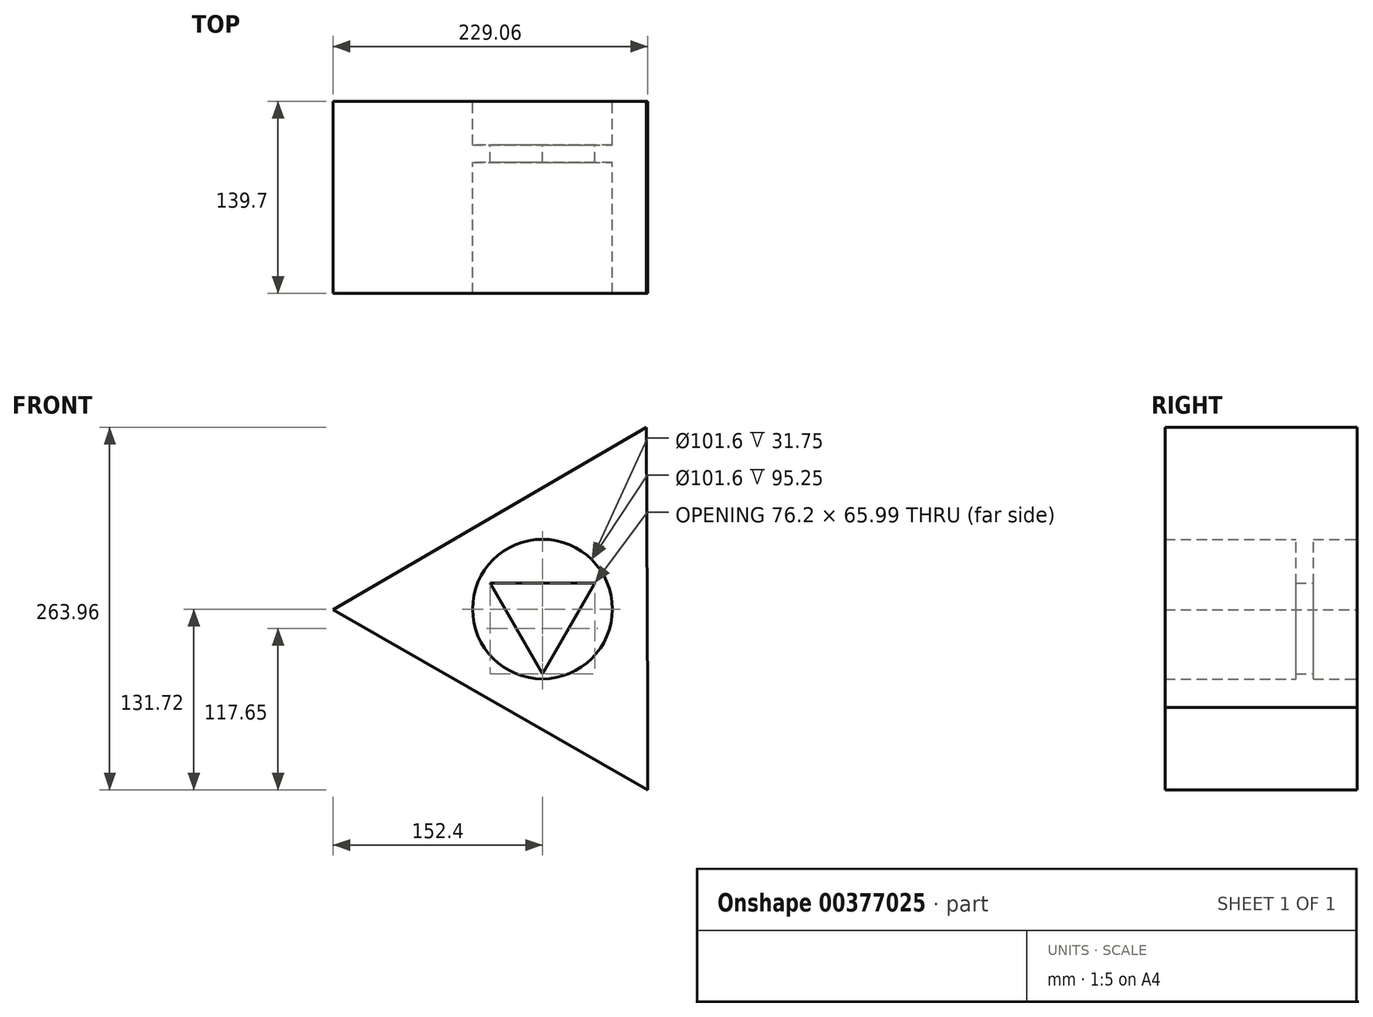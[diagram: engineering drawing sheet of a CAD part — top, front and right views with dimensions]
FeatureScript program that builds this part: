
annotation { "Feature Type Name" : "Feature", "Feature Type Description" : "" }
export const myFeature = defineFeature(function(context is Context, id is Id, definition is map)
    precondition{}
    {
        {
            var Q0;
            Q0=qCreatedBy(makeId("Front.planeOp"),FACE);
            var sketch = newSketch(context, id + "F0", { "sketchPlane" : qUnion([Q0])});
            skCircle(sketch, "E0.cCircle", {"center": v(0, 0) * mm, "radius": 76.2 * mm, "construction": true});
            skLineSegment(sketch, "E0.0", {"start": v(-152.4, -0.53) * mm, "end": v(75.74, 132.24) * mm});
            skLineSegment(sketch, "E0.1", {"start": v(75.74, 132.24) * mm, "end": v(76.66, -131.72) * mm});
            skLineSegment(sketch, "E0.2", {"start": v(76.66, -131.72) * mm, "end": v(-152.4, -0.53) * mm});
            skPoint(sketch, "E0.0.midPoint", {"position": v(-38.33, 65.86) * mm});
            skCircle(sketch, "E1", {"center": v(0, 0) * mm, "radius": 50.8 * mm});
            skArc(sketch, "E2", {"start": v(-129.9, -3.05) * mm, "mid": v(-125.48, 13.38) * mm, "end": v(-110.55, 21.54) * mm});
            skArc(sketch, "E3", {"start": v(-119.54, -19.35) * mm, "mid": v(-127.75, -11.18) * mm, "end": v(-130.76, 0) * mm});
            skArc(sketch, "E4", {"start": v(-119.54, -19.35) * mm, "mid": v(-114.2, -21.54) * mm, "end": v(-108.46, -22.3) * mm});
            skCircle(sketch, "E5.cCircle", {"center": v(0, -3.07) * mm, "radius": 22 * mm, "construction": true});
            skLineSegment(sketch, "E5.0", {"start": v(-38.1, 18.93) * mm, "end": v(38.1, 18.93) * mm});
            skLineSegment(sketch, "E5.1", {"start": v(38.1, 18.93) * mm, "end": v(0, -47.07) * mm});
            skLineSegment(sketch, "E5.2", {"start": v(0, -47.07) * mm, "end": v(-38.1, 18.93) * mm});
            skPoint(sketch, "E5.0.midPoint", {"position": v(0, 18.93) * mm});
            skFitSpline(sketch, "E6", {"points": [v(75.87, 94.92) * mm, v(22.34, 101.16) * mm], "startDerivative": vector(0.18, -52.74) * mm, "endDerivative": vector(62.41, 36.32) * mm});
            skLineSegment(sketch, "E7.bottom", {"start": v(76.54, -97.12) * mm, "end": v(25.74, -97.12) * mm});
            skLineSegment(sketch, "E7.top", {"start": v(76.54, -71.72) * mm, "end": v(25.74, -71.72) * mm});
            skLineSegment(sketch, "E7.left", {"start": v(76.54, -97.12) * mm, "end": v(76.54, -71.72) * mm});
            skLineSegment(sketch, "E7.right", {"start": v(25.74, -97.12) * mm, "end": v(25.74, -71.72) * mm});
            skSolve(sketch);
        }
        {
            var Q0;
            Q0=makeQuery(id+"F0.imprint","IMPRINT",FACE,{"disambiguationData":[TD([[makeQuery(id+"F0.imprint","IMPRINT",EDGE,{"derivedFrom":sQuery(id+"F0.wireOp",EDGE,"E1")}),1.0]])]});
            extrude(context, id + "F1", {"entities" : qUnion([Q0]), "endBound" : BoundingType.SYMMETRIC, "depth" : 12.7 * mm});
        }
        {
            var Q0;
            Q0 = qSketchRegion(id + "F0", true);
            extrude(context, id + "F2", {"entities" : qUnion([Q0]), "operationType" : NewBodyOperationType.ADD, "endBound" : BoundingType.SYMMETRIC, "depth" : 76.2 * mm});
        }
        {
            var Q0;
            Q0=makeQuery(id+"F2.opExtrude","CAP_FACE",FACE,{"disambiguationData":[OSD([sQuery(id+"F0.wireOp",EDGE,"E0.0"),sQuery(id+"F0.wireOp",EDGE,"E0.1"),sQuery(id+"F0.wireOp",EDGE,"E0.2"),sQuery(id+"F0.wireOp",EDGE,"E1"),sQuery(id+"F0.wireOp",EDGE,"E7.top"),sQuery(id+"F0.wireOp",EDGE,"E7.left")])],"isStart":false});
            extrude(context, id + "F3", {"entities" : qUnion([Q0]), "operationType" : NewBodyOperationType.ADD, "endBound" : BoundingType.SYMMETRIC, "depth" : 127 * mm});
        }
    });
